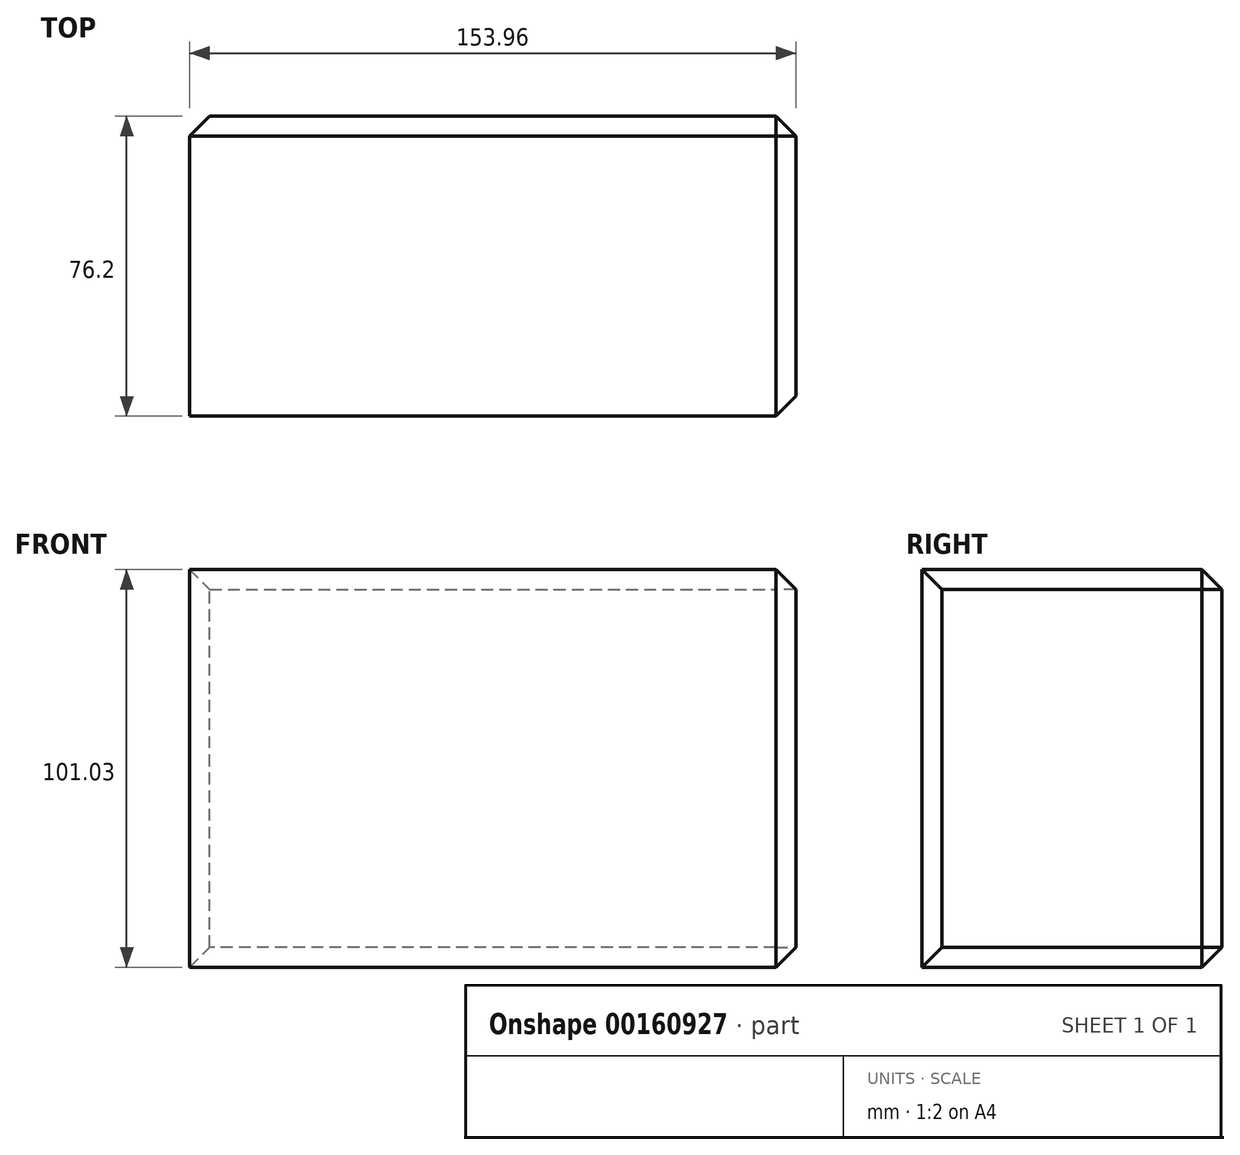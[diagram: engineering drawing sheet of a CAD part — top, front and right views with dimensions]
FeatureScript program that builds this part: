
annotation { "Feature Type Name" : "Feature", "Feature Type Description" : "" }
export const myFeature = defineFeature(function(context is Context, id is Id, definition is map)
    precondition{}
    {
        {
            var Q0;
            Q0=qCreatedBy(makeId("Front.planeOp"),FACE);
            var sketch = newSketch(context, id + "F0", { "sketchPlane" : qUnion([Q0])});
            skLineSegment(sketch, "E0.bottom", {"start": v(-76.98, 44.38) * mm, "end": v(76.98, 44.38) * mm});
            skLineSegment(sketch, "E0.top", {"start": v(-76.98, -44.38) * mm, "end": v(76.98, -44.38) * mm});
            skLineSegment(sketch, "E0.left", {"start": v(-76.98, 44.38) * mm, "end": v(-76.98, -44.38) * mm});
            skLineSegment(sketch, "E0.right", {"start": v(76.98, 44.38) * mm, "end": v(76.98, -44.38) * mm});
            skPoint(sketch, "E0.middle", {"position": v(0, 0) * mm});
            skLineSegment(sketch, "E1.0", {"start": v(-76.98, 73.6) * mm, "end": v(76.98, 73.6) * mm});
            skLineSegment(sketch, "E2.bottom", {"start": v(-76.98, 32.12) * mm, "end": v(76.98, 32.12) * mm});
            skLineSegment(sketch, "E2.top", {"start": v(-76.98, -56.65) * mm, "end": v(76.98, -56.65) * mm});
            skLineSegment(sketch, "E2.left", {"start": v(-76.98, 32.12) * mm, "end": v(-76.98, -56.65) * mm});
            skLineSegment(sketch, "E2.right", {"start": v(76.98, 32.12) * mm, "end": v(76.98, -56.65) * mm});
            skPoint(sketch, "E2.middle", {"position": v(0, -12.27) * mm});
            skLineSegment(sketch, "E3.0", {"start": v(-76.98, 61.33) * mm, "end": v(76.98, 61.33) * mm});
            skSolve(sketch);
        }
        {
            var Q0;
            Q0 = qSketchRegion(id + "F0", true);
            extrude(context, id + "F1", {"entities" : qUnion([Q0]), "depth" : 76.2 * mm});
        }
        {
            var Q0;
            Q0=makeQuery(id+"F1.opExtrude","CAP_EDGE",EDGE,{"disambiguationData":[OSD([sQuery(id+"F0.wireOp",EDGE,"E2.top")])],"isStart":true});
            var Q1;
            Q1=makeQuery(id+"F1.opExtrude","CAP_FACE",FACE,{"disambiguationData":[OSD([sQuery(id+"F0.wireOp",EDGE,"E0.bottom"),sQuery(id+"F0.wireOp",EDGE,"E0.left"),sQuery(id+"F0.wireOp",EDGE,"E0.right"),sQuery(id+"F0.wireOp",EDGE,"E2.top"),sQuery(id+"F0.wireOp",EDGE,"E2.left"),sQuery(id+"F0.wireOp",EDGE,"E2.right")])],"isStart":true});
            var Q2;
            Q2=makeQuery(id+"F1.opExtrude","SWEPT_FACE",FACE,{"disambiguationData":[OSD([sQuery(id+"F0.wireOp",EDGE,"E0.right"),sQuery(id+"F0.wireOp",EDGE,"E2.right")])]});
            chamfer(context, id + "F2", {"entities" : qUnion([Q0, Q1, Q2]), "width" : 5.08 * mm, "tangentPropagation" : true});
        }
    });
